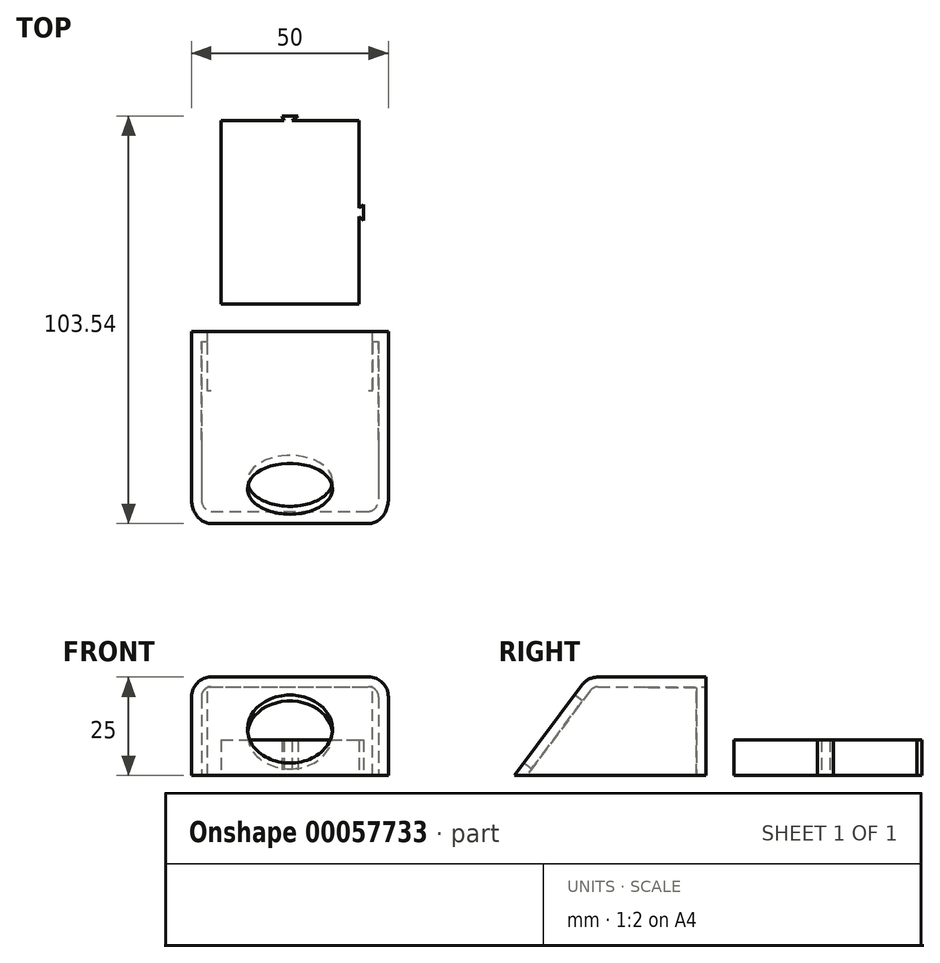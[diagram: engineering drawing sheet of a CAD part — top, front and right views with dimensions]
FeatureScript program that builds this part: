
annotation { "Feature Type Name" : "Feature", "Feature Type Description" : "" }
export const myFeature = defineFeature(function(context is Context, id is Id, definition is map)
    precondition{}
    {
        {
            var Q0;
            Q0=qCreatedBy(makeId("Top.planeOp"),FACE);
            var sketch = newSketch(context, id + "F0", { "sketchPlane" : qUnion([Q0])});
            skLineSegment(sketch, "E0.bottom", {"start": v(-25, 15) * mm, "end": v(25, 15) * mm});
            skLineSegment(sketch, "E0.top", {"start": v(-25, -15) * mm, "end": v(25, -15) * mm});
            skLineSegment(sketch, "E0.left", {"start": v(-25, 15) * mm, "end": v(-25, -15) * mm});
            skLineSegment(sketch, "E0.right", {"start": v(25, 15) * mm, "end": v(25, -15) * mm});
            skSolve(sketch);
        }
        {
            var Q0;
            Q0=makeQuery(id+"F0.imprint","IMPRINT",FACE,{"disambiguationData":[TD([[makeQuery(id+"F0.imprint","IMPRINT",EDGE,{"derivedFrom":sQuery(id+"F0.wireOp",EDGE,"E0.bottom")}),-1.0]])]});
            extrude(context, id + "F1", {"entities" : qUnion([Q0]), "depth" : 25 * mm});
        }
        {
            var Q0;
            Q0=makeQuery(id+"F1.opExtrude","SWEPT_FACE",FACE,{"disambiguationData":[OSD([sQuery(id+"F0.wireOp",EDGE,"E0.right")])]});
            var sketch = newSketch(context, id + "F2", { "sketchPlane" : qUnion([Q0])});
            skLineSegment(sketch, "E1", {"start": v(-15, 25) * mm, "end": v(-33.74, 0) * mm});
            skLineSegment(sketch, "E2", {"start": v(-33.74, 0) * mm, "end": v(-15, 0) * mm});
            skSolve(sketch);
        }
        {
            var Q0;
            Q0=makeQuery(id+"F2.imprint","IMPRINT",FACE,{"disambiguationData":[TD([[makeQuery(id+"F2.imprint","IMPRINT",EDGE,{"derivedFrom":sQuery(id+"F2.wireOp",EDGE,"E1")}),1.0]])]});
            var Q1;
            Q1=makeQuery(id+"F1.opExtrude","SWEPT_FACE",FACE,{"disambiguationData":[OSD([sQuery(id+"F0.wireOp",EDGE,"E0.left")])]});
            extrude(context, id + "F3", {"entities" : qUnion([Q0]), "endBound" : BoundingType.UP_TO_SURFACE, "oppositeDirection" : true, "endBoundEntityFace" : qUnion([Q1]), "depth" : 25 * mm});
        }
        {
            var Q0;
            Q0=makeQuery(id+"F1.opExtrude","SWEPT_BODY",BODY,{"disambiguationData":[OSD([sQuery(id+"F0.wireOp",EDGE,"E0.bottom"),sQuery(id+"F0.wireOp",EDGE,"E0.top"),sQuery(id+"F0.wireOp",EDGE,"E0.left"),sQuery(id+"F0.wireOp",EDGE,"E0.right")])]});
            var Q1;
            Q1=makeQuery(id+"F3.opExtrude","SWEPT_BODY",BODY,{"disambiguationData":[OSD([sQuery(id+"F0.wireOp",EDGE,"E0.top"),sQuery(id+"F0.wireOp",EDGE,"E0.right"),sQuery(id+"F2.wireOp",EDGE,"E1"),sQuery(id+"F2.wireOp",EDGE,"E2")])]});
            booleanBodies(context, id + "F4", {"operationType" : BooleanOperationType.UNION, "tools" : qUnion([Q0, Q1])});
        }
        {
            var Q0;
            Q0=makeQuery(id+"F3.opExtrude","CAP_EDGE",EDGE,{"disambiguationData":[OSD([sQuery(id+"F2.wireOp",EDGE,"E1")])],"isStart":true});
            var Q1;
            Q1=makeQuery(id+"F3.opExtrude","CAP_EDGE",EDGE,{"disambiguationData":[OSD([sQuery(id+"F2.wireOp",EDGE,"E1")])],"isStart":false});
            var Q2;
            {var subQ0=sQuery(id+"F0.wireOp",EDGE,"E0.top");Q2=makeQuery(id+"F4.opBoolean","MERGE",EDGE,{"derivedFrom":[makeQuery(id+"F1.opExtrude","CAP_EDGE",EDGE,{"disambiguationData":[OSD([subQ0])],"isStart":false}),makeQuery(id+"F3.opExtrude","SWEPT_EDGE",EDGE,{"disambiguationData":[OSD([subQ0,sQuery(id+"F0.wireOp",EDGE,"E0.right"),sQuery(id+"F2.wireOp",EDGE,"E1")])]})]});}
            var Q3;
            Q3=makeQuery(id+"F1.opExtrude","CAP_EDGE",EDGE,{"disambiguationData":[OSD([sQuery(id+"F0.wireOp",EDGE,"E0.right")])],"isStart":false});
            var Q4;
            Q4=makeQuery(id+"F1.opExtrude","CAP_EDGE",EDGE,{"disambiguationData":[OSD([sQuery(id+"F0.wireOp",EDGE,"E0.left")])],"isStart":false});
            fillet(context, id + "F5", {"entities" : qUnion([Q0, Q1, Q2, Q3, Q4]), "radius" : 5 * mm, "tangentPropagation" : true, "allowEdgeOverflow" : false});
        }
        {
            var Q0;
            Q0=makeQuery(id+"F4.opBoolean","MERGE",FACE,{"derivedFrom":[makeQuery(id+"F1.opExtrude","CAP_FACE",FACE,{"disambiguationData":[OSD([sQuery(id+"F0.wireOp",EDGE,"E0.bottom"),sQuery(id+"F0.wireOp",EDGE,"E0.top"),sQuery(id+"F0.wireOp",EDGE,"E0.left"),sQuery(id+"F0.wireOp",EDGE,"E0.right")])],"isStart":true}),makeQuery(id+"F3.opExtrude","SWEPT_FACE",FACE,{"disambiguationData":[OSD([sQuery(id+"F2.wireOp",EDGE,"E2")])]})]});
            shell(context, id + "F6", {"entities" : qUnion([Q0]), "thickness" : 2.5 * mm});
        }
        {
            var Q0;
            Q0=makeQuery(id+"F3.opExtrude","SWEPT_FACE",FACE,{"disambiguationData":[OSD([sQuery(id+"F2.wireOp",EDGE,"E1")])]});
            var sketch = newSketch(context, id + "F7", { "sketchPlane" : qUnion([Q0])});
            skCircle(sketch, "E3", {"center": v(0, -5.5) * mm, "radius": 10.8 * mm});
            skSolve(sketch);
        }
        {
            var Q0;
            Q0 = qSketchRegion(id + "F7", true);
            extrude(context, id + "F8", {"entities" : qUnion([Q0]), "operationType" : NewBodyOperationType.REMOVE, "oppositeDirection" : true, "depth" : 25 * mm});
        }
        {
            var Q0;
            Q0=qCreatedBy(makeId("Top.planeOp"),FACE);
            var sketch = newSketch(context, id + "F9", { "sketchPlane" : qUnion([Q0])});
            skLineSegment(sketch, "E4.bottom", {"start": v(-17.5, 22) * mm, "end": v(17.5, 22) * mm});
            skLineSegment(sketch, "E4.top", {"start": v(-17.5, 68.6) * mm, "end": v(17.5, 68.6) * mm});
            skLineSegment(sketch, "E4.left", {"start": v(-17.5, 22) * mm, "end": v(-17.5, 68.6) * mm});
            skLineSegment(sketch, "E4.right", {"start": v(17.5, 22) * mm, "end": v(17.5, 68.6) * mm});
            skLineSegment(sketch, "E5", {"start": v(22.18, 45.3) * mm, "end": v(-29.67, 45.3) * mm, "construction": true});
            skLineSegment(sketch, "E6", {"start": v(17.5, 44.3) * mm, "end": v(18.7, 43.3) * mm});
            skLineSegment(sketch, "E7", {"start": v(18.7, 43.3) * mm, "end": v(18.7, 47.3) * mm});
            skLineSegment(sketch, "E8", {"start": v(18.7, 47.3) * mm, "end": v(17.5, 46.45) * mm});
            skLineSegment(sketch, "E9", {"start": v(0, 19.5) * mm, "end": v(0, 72.59) * mm, "construction": true});
            skLineSegment(sketch, "E10", {"start": v(2, 69.8) * mm, "end": v(-2, 69.8) * mm});
            skLineSegment(sketch, "E11", {"start": v(2, 69.8) * mm, "end": v(0.55, 68.6) * mm});
            skLineSegment(sketch, "E12", {"start": v(-2, 69.8) * mm, "end": v(-1.45, 68.6) * mm});
            skSolve(sketch);
        }
        {
            var Q0;
            Q0 = qSketchRegion(id + "F9", true);
            extrude(context, id + "F10", {"entities" : qUnion([Q0]), "depth" : 9 * mm});
        }
        {
            var Q0;
            Q0=qCreatedBy(makeId("Top.planeOp"),FACE);
            var sketch = newSketch(context, id + "F11", { "sketchPlane" : qUnion([Q0])});
            skLineSegment(sketch, "E13.bottom", {"start": v(21, 0) * mm, "end": v(-21, 0) * mm});
            skLineSegment(sketch, "E13.top", {"start": v(21, 73.17) * mm, "end": v(-21, 73.17) * mm});
            skLineSegment(sketch, "E13.left", {"start": v(21, 0) * mm, "end": v(21, 73.17) * mm});
            skLineSegment(sketch, "E13.right", {"start": v(-21, 0) * mm, "end": v(-21, 73.17) * mm});
            skSolve(sketch);
        }
        {
            var Q0;
            Q0 = qSketchRegion(id + "F11", true);
            var Q1;
            Q1=makeQuery(id+"F6.opShell","OFFSET_FACE",FACE,{"disambiguationData":[OSD([sQuery(id+"F0.wireOp",EDGE,"E0.bottom"),sQuery(id+"F0.wireOp",EDGE,"E0.top"),sQuery(id+"F0.wireOp",EDGE,"E0.left"),sQuery(id+"F0.wireOp",EDGE,"E0.right")])]});
            extrude(context, id + "F12", {"entities" : qUnion([Q0]), "endBound" : BoundingType.UP_TO_SURFACE, "endBoundEntityFace" : qUnion([Q1]), "depth" : 18 * mm});
        }
        {
            var Q0;
            Q0=makeQuery(id+"F12.opExtrude","SWEPT_BODY",BODY,{"disambiguationData":[OSD([sQuery(id+"F11.wireOp",EDGE,"E13.bottom"),sQuery(id+"F11.wireOp",EDGE,"E13.top"),sQuery(id+"F11.wireOp",EDGE,"E13.left"),sQuery(id+"F11.wireOp",EDGE,"E13.right")])]});
            var Q1;
            Q1=makeQuery(id+"F1.opExtrude","SWEPT_BODY",BODY,{"disambiguationData":[OSD([sQuery(id+"F0.wireOp",EDGE,"E0.bottom"),sQuery(id+"F0.wireOp",EDGE,"E0.top"),sQuery(id+"F0.wireOp",EDGE,"E0.left"),sQuery(id+"F0.wireOp",EDGE,"E0.right")])]});
            booleanBodies(context, id + "F13", {"operationType" : BooleanOperationType.SUBTRACTION, "tools" : qUnion([Q0]), "targets" : qUnion([Q1])});
        }
        {
            var Q0;
            Q0=makeQuery(id+"F1.opExtrude","SWEPT_BODY",BODY,{"disambiguationData":[OSD([sQuery(id+"F0.wireOp",EDGE,"E0.bottom"),sQuery(id+"F0.wireOp",EDGE,"E0.top"),sQuery(id+"F0.wireOp",EDGE,"E0.left"),sQuery(id+"F0.wireOp",EDGE,"E0.right")])]});
            transform(context, id + "F14", {"entities" : qUnion([Q0]), "transformType" : TransformType.TRANSLATION_3D, "dx" : 0 * mm, "dy" : 0 * mm, "dz" : 0 * mm, "makeCopy" : true});
        }
    });
